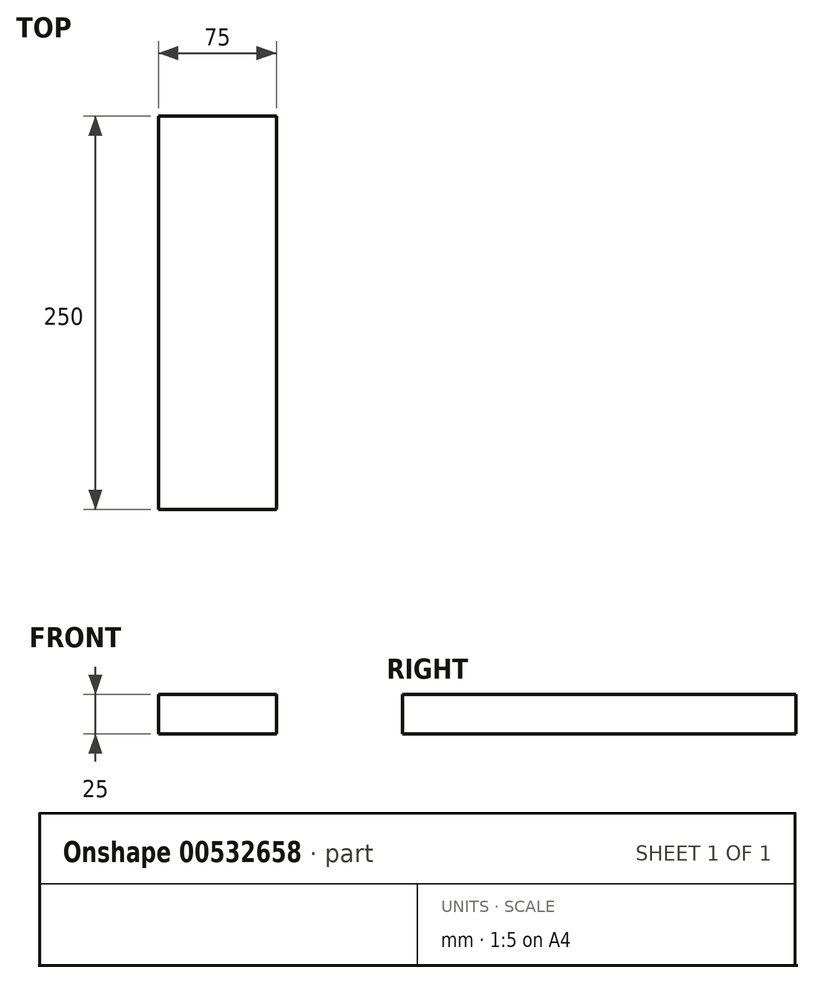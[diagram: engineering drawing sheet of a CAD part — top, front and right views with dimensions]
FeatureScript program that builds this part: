
annotation { "Feature Type Name" : "Feature", "Feature Type Description" : "" }
export const myFeature = defineFeature(function(context is Context, id is Id, definition is map)
    precondition{}
    {
        {
            var Q0;
            Q0=qCreatedBy(makeId("Front.planeOp"),FACE);
            var sketch = newSketch(context, id + "F0", { "sketchPlane" : qUnion([Q0])});
            skLineSegment(sketch, "E0.bottom", {"start": v(-44.2, 4.62) * mm, "end": v(30.8, 4.62) * mm});
            skLineSegment(sketch, "E0.top", {"start": v(-44.2, -20.38) * mm, "end": v(30.8, -20.38) * mm});
            skLineSegment(sketch, "E0.left", {"start": v(-44.2, 4.62) * mm, "end": v(-44.2, -20.38) * mm});
            skLineSegment(sketch, "E0.right", {"start": v(30.8, 4.62) * mm, "end": v(30.8, -20.38) * mm});
            skSolve(sketch);
        }
        {
            var Q0;
            Q0=qSketchRegion(id+"F0",true);
            extrude(context, id + "F1", {"entities" : qUnion([Q0]), "oppositeDirection" : true, "depth" : 250 * mm, "offsetDistance" : 25 * mm});
        }
    });
